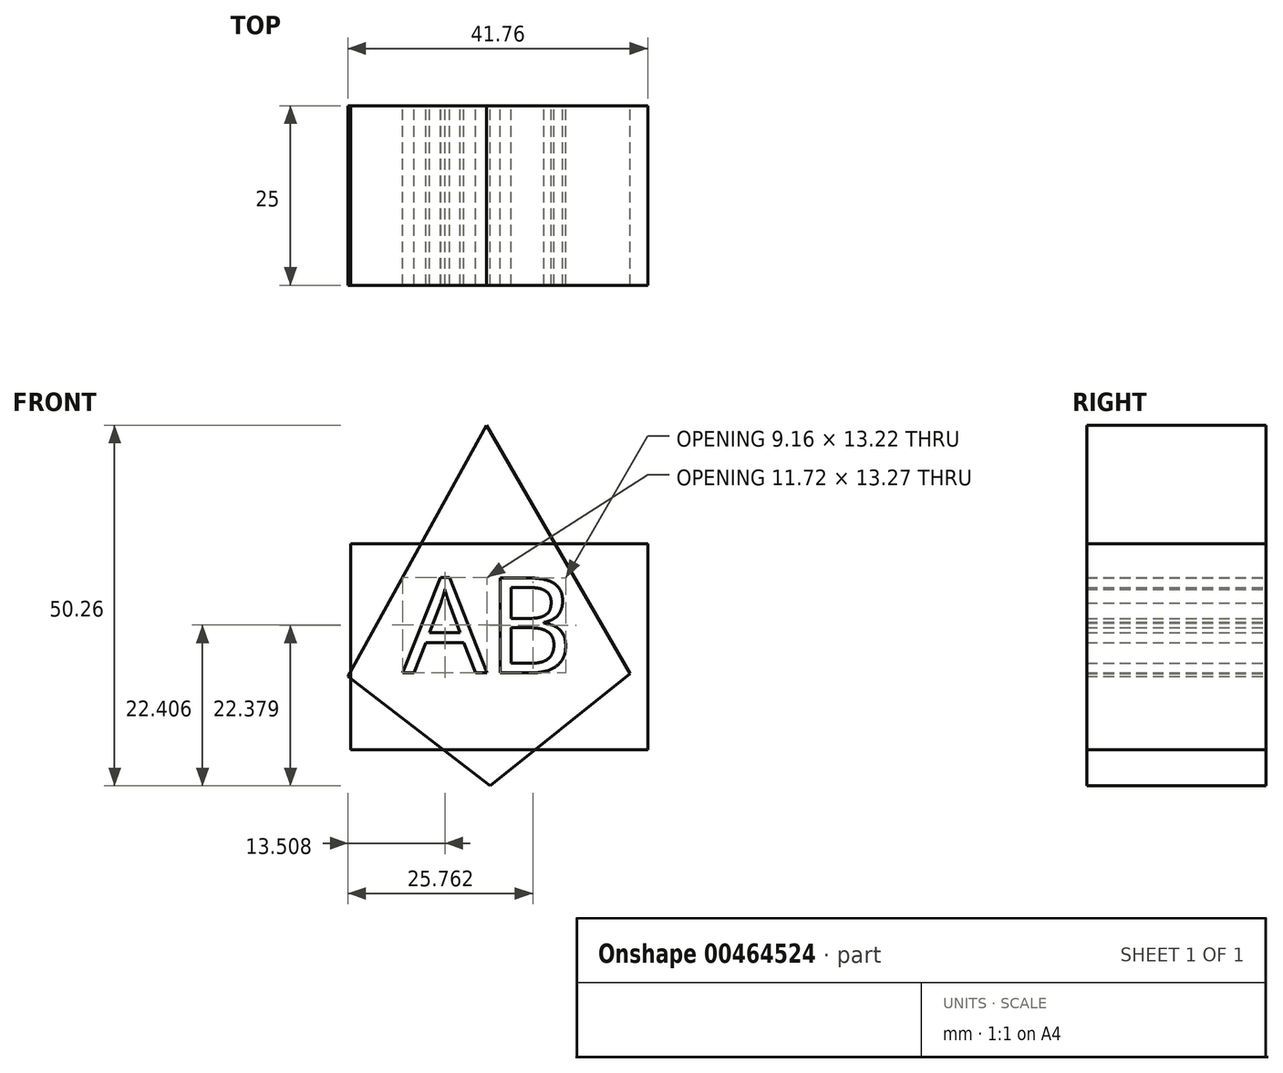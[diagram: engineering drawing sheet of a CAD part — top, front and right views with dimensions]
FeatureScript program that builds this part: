
annotation { "Feature Type Name" : "Feature", "Feature Type Description" : "" }
export const myFeature = defineFeature(function(context is Context, id is Id, definition is map)
    precondition{}
    {
        {
            var Q0;
            Q0=qCreatedBy(makeId("Front.planeOp"),FACE);
            var sketch = newSketch(context, id + "F0", { "sketchPlane" : qUnion([Q0])});
            skLineSegment(sketch, "E0", {"start": v(-39.33, -0.38) * mm, "end": v(-20, 34.64) * mm});
            skLineSegment(sketch, "E1", {"start": v(-20, 34.64) * mm, "end": v(0, 0) * mm});
            skText(sketch, "E2", { "text": "AB", "fontName": "OpenSans-Regular.ttf"});
            skLineSegment(sketch, "E3", {"start": v(-39.33, -0.38) * mm, "end": v(-19.52, -15.62) * mm});
            skLineSegment(sketch, "E4", {"start": v(-19.52, -15.62) * mm, "end": v(0, 0) * mm});
            const initialGuessF0  = {"E2": [-0.03168, 0.00015, 1, 0, 0.01333]};
            skSetInitialGuess(sketch, initialGuessF0);
            skSolve(sketch);
        }
        {
            var Q0;
            Q0=makeQuery(id+"F0.imprint","IMPRINT",FACE,{"disambiguationData":[TD([[makeQuery(id+"F0.imprint","IMPRINT",EDGE,{"derivedFrom":sQuery(id+"F0.wireOp",EDGE,"E0")}),-1.0]])]});
            var Q1;
            Q1=makeQuery(id+"F0.imprint","IMPRINT",FACE,{"disambiguationData":[TD([[makeQuery(id+"F0.imprint","IMPRINT",EDGE,{"derivedFrom":sQuery(id+"F0.wireOp",EDGE,"E2.sketch_text.stroke-8")}),1.0]])]});
            var Q2;
            Q2=makeQuery(id+"F0.imprint","IMPRINT",FACE,{"disambiguationData":[TD([[makeQuery(id+"F0.imprint","IMPRINT",EDGE,{"derivedFrom":sQuery(id+"F0.wireOp",EDGE,"E2.sketch_text.stroke-24")}),1.0]])]});
            var Q3;
            Q3=makeQuery(id+"F0.imprint","IMPRINT",FACE,{"disambiguationData":[TD([[makeQuery(id+"F0.imprint","IMPRINT",EDGE,{"derivedFrom":sQuery(id+"F0.wireOp",EDGE,"E2.sketch_text.stroke-31")}),1.0]])]});
            extrude(context, id + "F1", {"entities" : qUnion([Q0, Q1, Q2, Q3]), "depth" : 25 * mm});
        }
        {
            var Q0;
            Q0=qCreatedBy(makeId("Front.planeOp"),FACE);
            var sketch = newSketch(context, id + "F2", { "sketchPlane" : qUnion([Q0])});
            skLineSegment(sketch, "E5.bottom", {"start": v(-38.97, 18.08) * mm, "end": v(2.43, 18.08) * mm});
            skLineSegment(sketch, "E5.top", {"start": v(-38.97, -10.61) * mm, "end": v(2.43, -10.61) * mm});
            skLineSegment(sketch, "E5.left", {"start": v(-38.97, 18.08) * mm, "end": v(-38.97, -10.61) * mm});
            skLineSegment(sketch, "E5.right", {"start": v(2.43, 18.08) * mm, "end": v(2.43, -10.61) * mm});
            skSolve(sketch);
        }
        {
            var Q0;
            Q0=makeQuery(id+"F2.imprint","IMPRINT",FACE,{"disambiguationData":[TD([[makeQuery(id+"F2.imprint","IMPRINT",EDGE,{"derivedFrom":sQuery(id+"F2.wireOp",EDGE,"E5.bottom")}),-1.0]])]});
            extrude(context, id + "F3", {"entities" : qUnion([Q0]), "depth" : 25 * mm});
        }
    });
